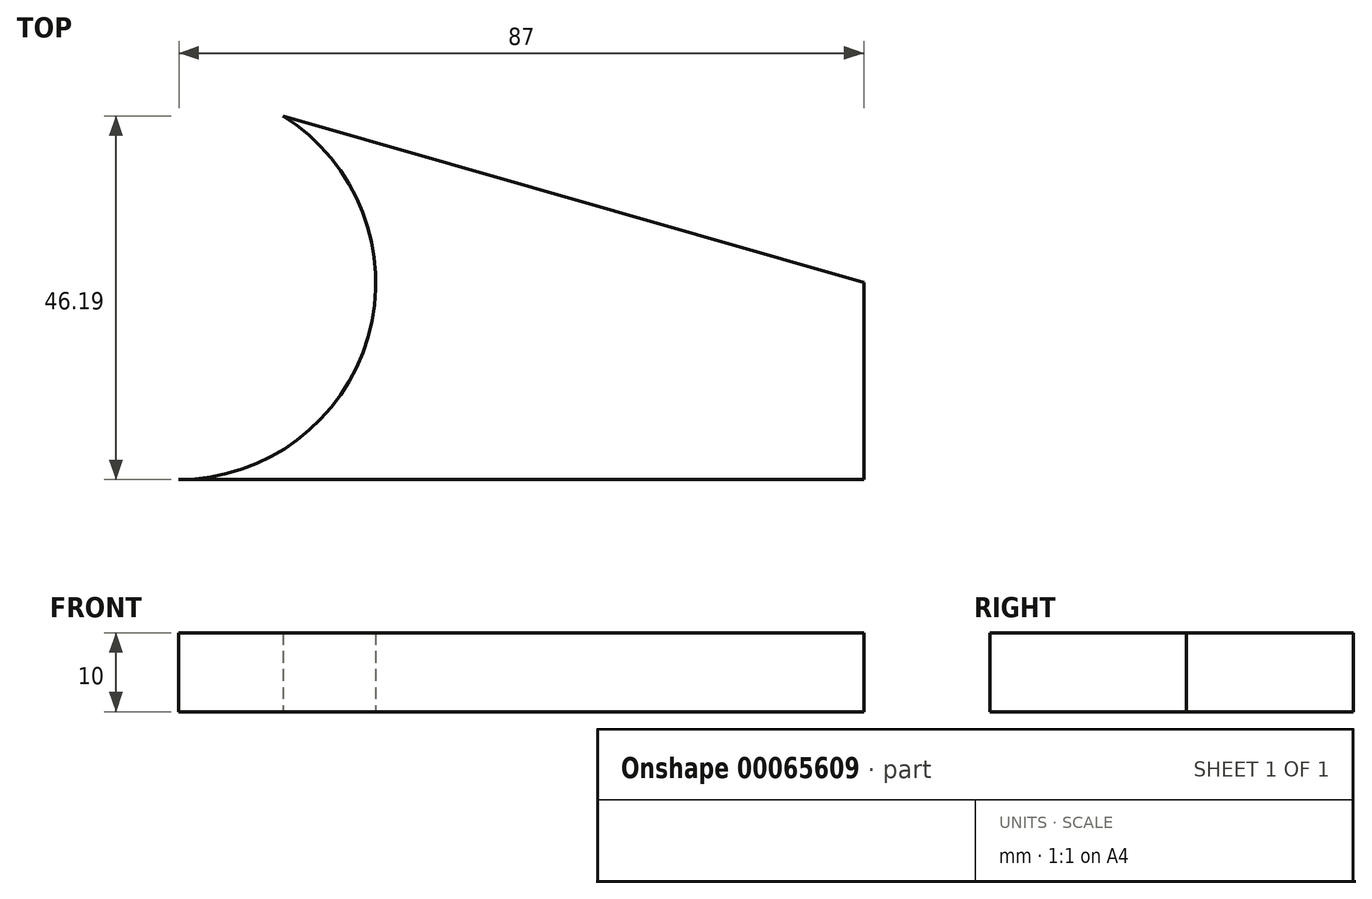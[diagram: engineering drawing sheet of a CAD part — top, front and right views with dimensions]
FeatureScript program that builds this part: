
annotation { "Feature Type Name" : "Feature", "Feature Type Description" : "" }
export const myFeature = defineFeature(function(context is Context, id is Id, definition is map)
    precondition{}
    {
        {
            var Q0;
            Q0=qCreatedBy(makeId("Top.planeOp"),FACE);
            var sketch = newSketch(context, id + "F0", { "sketchPlane" : qUnion([Q0])});
            skLineSegment(sketch, "E0", {"start": v(-40.22, 22.6) * mm, "end": v(-40.22, -27.4) * mm});
            skLineSegment(sketch, "E1", {"start": v(-40.22, -27.4) * mm, "end": v(46.78, -27.4) * mm});
            skLineSegment(sketch, "E2", {"start": v(46.78, -27.4) * mm, "end": v(46.78, -2.4) * mm});
            skLineSegment(sketch, "E3", {"start": v(46.78, -2.4) * mm, "end": v(-40.22, 22.6) * mm});
            skSolve(sketch);
        }
        {
            var Q0;
            Q0=makeQuery(id+"F0.imprint","IMPRINT",FACE,{"disambiguationData":[TD([[makeQuery(id+"F0.imprint","IMPRINT",EDGE,{"derivedFrom":sQuery(id+"F0.wireOp",EDGE,"E0")}),1.0]])]});
            extrude(context, id + "F1", {"entities" : qUnion([Q0]), "endBound" : BoundingType.SYMMETRIC, "depth" : 10 * mm});
        }
        {
            var Q0;
            Q0=makeQuery(id+"F1.opExtrude","CAP_FACE",FACE,{"disambiguationData":[OSD([sQuery(id+"F0.wireOp",EDGE,"E0"),sQuery(id+"F0.wireOp",EDGE,"E1"),sQuery(id+"F0.wireOp",EDGE,"E2"),sQuery(id+"F0.wireOp",EDGE,"E3")])],"isStart":true});
            var sketch = newSketch(context, id + "F2", { "sketchPlane" : qUnion([Q0])});
            skArc(sketch, "E4", {"start": v(-40.22, -22.6) * mm, "mid": v(-15.22, 2.4) * mm, "end": v(-40.22, 27.4) * mm});
            skSolve(sketch);
        }
        {
            var Q0;
            {var subQ1=makeQuery(id+"F1.opExtrude","CAP_EDGE",EDGE,{"disambiguationData":[OSD([sQuery(id+"F0.wireOp",EDGE,"E0")])],"isStart":true});Q0=makeQuery(id+"F2.imprint","IMPRINT",FACE,{"disambiguationData":[TD([[makeQuery(id+"F2.imprint","IMPRINT",EDGE,{"derivedFrom":subQ1}),-1.0]])]});}
            extrude(context, id + "F3", {"entities" : qUnion([Q0]), "operationType" : NewBodyOperationType.REMOVE, "oppositeDirection" : true, "depth" : 25 * mm});
        }
    });
